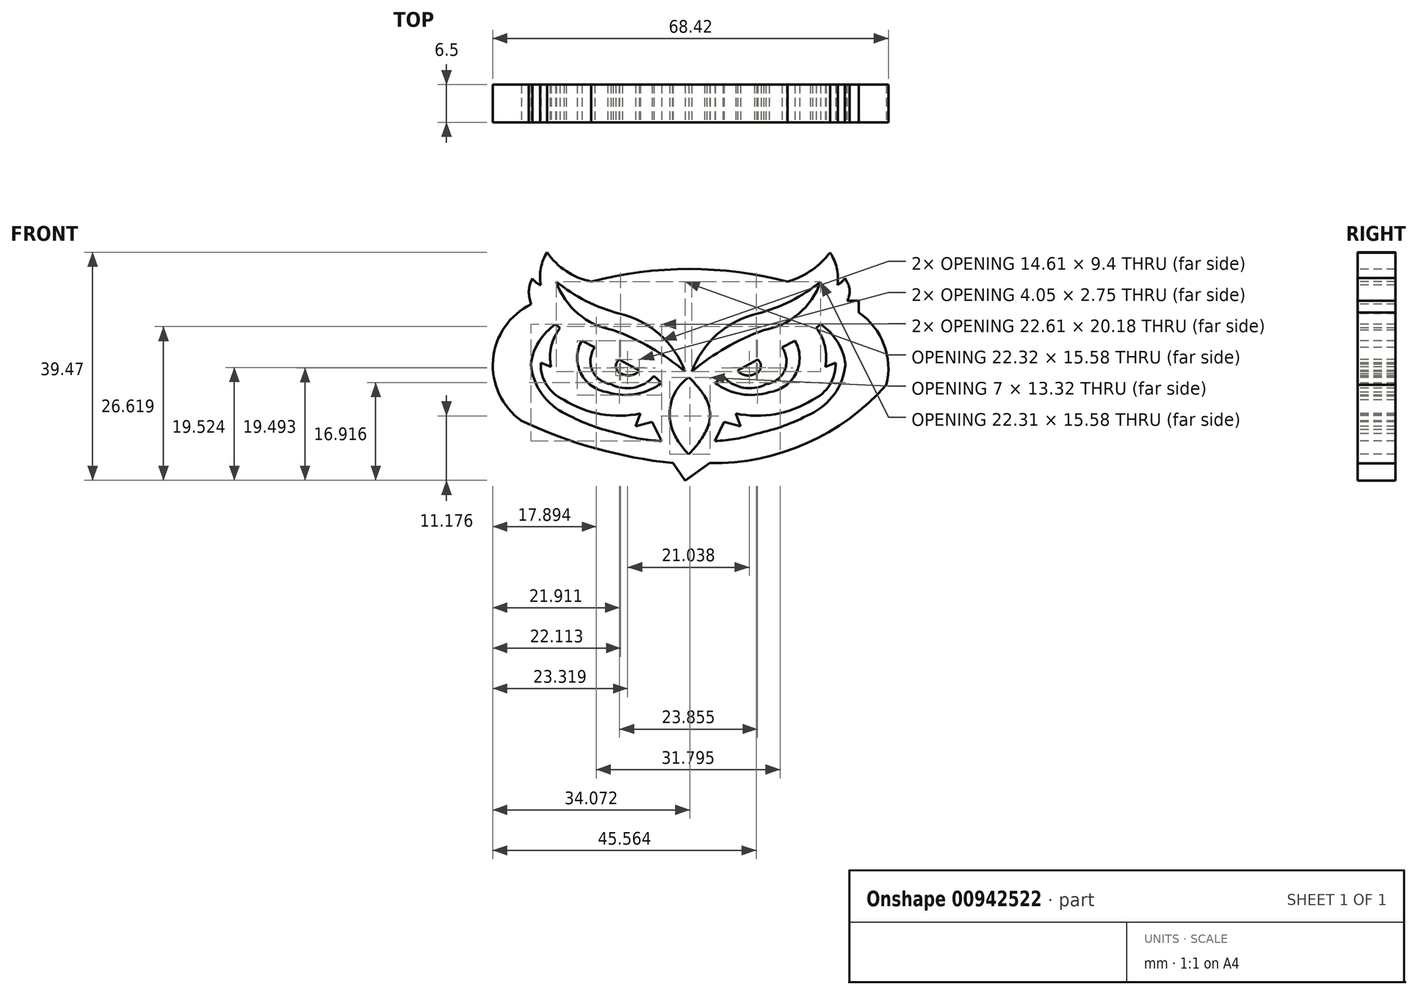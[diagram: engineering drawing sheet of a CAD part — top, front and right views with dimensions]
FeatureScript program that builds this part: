
annotation { "Feature Type Name" : "Feature", "Feature Type Description" : "" }
export const myFeature = defineFeature(function(context is Context, id is Id, definition is map)
    precondition{}
    {
        {
            var Q0;
            Q0=qCreatedBy(makeId("Front.planeOp"),FACE);
            var sketch = newSketch(context, id + "F0", { "sketchPlane" : qUnion([Q0])});
            skArc(sketch, "E0", {"start": v(-26.6, 12.43) * mm, "mid": v(-33.23, 2.83) * mm, "end": v(-28.3, -7.74) * mm});
            skArc(sketch, "E1", {"start": v(-28.3, -7.74) * mm, "mid": v(-15.5, -12.5) * mm, "end": v(-2.1, -15.07) * mm});
            skLineSegment(sketch, "E2", {"start": v(-2.1, -15.07) * mm, "end": v(0, -18.05) * mm});
            skLineSegment(sketch, "E3", {"start": v(0, -18.05) * mm, "end": v(4.24, -15.07) * mm});
            skArc(sketch, "E4", {"start": v(4.24, -15.07) * mm, "mid": v(21.01, -11.63) * mm, "end": v(34.81, -1.5) * mm});
            skArc(sketch, "E5", {"start": v(34.81, -1.5) * mm, "mid": v(34.38, 5.5) * mm, "end": v(30.06, 11) * mm});
            skLineSegment(sketch, "E6", {"start": v(30.06, 11) * mm, "end": v(30.06, 13.03) * mm});
            skLineSegment(sketch, "E7", {"start": v(30.06, 13.03) * mm, "end": v(28.03, 13.03) * mm});
            skArc(sketch, "E8", {"start": v(28.03, 13.03) * mm, "mid": v(28.46, 14.66) * mm, "end": v(28.03, 16.29) * mm});
            skLineSegment(sketch, "E9", {"start": v(28.03, 16.29) * mm, "end": v(27.65, 16.94) * mm});
            skArc(sketch, "E10", {"start": v(26.34, 15.79) * mm, "mid": v(27.07, 16.28) * mm, "end": v(27.65, 16.94) * mm});
            skArc(sketch, "E11", {"start": v(26.34, 15.79) * mm, "mid": v(26.23, 18.7) * mm, "end": v(25.06, 21.37) * mm});
            skArc(sketch, "E12", {"start": v(18.13, 16.5) * mm, "mid": v(21.98, 18.39) * mm, "end": v(25.06, 21.37) * mm});
            skLineSegment(sketch, "E13", {"start": v(18.13, 16.5) * mm, "end": v(17.7, 16.36) * mm});
            skArc(sketch, "E14", {"start": v(17.7, 16.36) * mm, "mid": v(0.72, 18.53) * mm, "end": v(-16.27, 16.36) * mm});
            skPoint(sketch, "E15", {"position": v(-26.6, 12.43) * mm});
            skArc(sketch, "E16", {"start": v(-26.44, 16.9) * mm, "mid": v(-27.02, 14.68) * mm, "end": v(-26.6, 12.43) * mm});
            skArc(sketch, "E17", {"start": v(-26.44, 16.9) * mm, "mid": v(-25.8, 16.21) * mm, "end": v(-24.98, 15.74) * mm});
            skArc(sketch, "E18", {"start": v(-23.87, 21.42) * mm, "mid": v(-24.96, 18.69) * mm, "end": v(-24.98, 15.74) * mm});
            skArc(sketch, "E19", {"start": v(-23.87, 21.42) * mm, "mid": v(-20.57, 18.14) * mm, "end": v(-16.27, 16.36) * mm});
            skArc(sketch, "E20", {"start": v(-22.31, 16.36) * mm, "mid": v(-17.14, 13) * mm, "end": v(-11.36, 10.82) * mm});
            skArc(sketch, "E21", {"start": v(0, 0.78) * mm, "mid": v(-4.42, 7.23) * mm, "end": v(-11.36, 10.82) * mm});
            skArc(sketch, "E22", {"start": v(0, 0.78) * mm, "mid": v(-5.9, 4.91) * mm, "end": v(-12.44, 7.97) * mm});
            skArc(sketch, "E23", {"start": v(-22.31, 16.36) * mm, "mid": v(-18.53, 10.81) * mm, "end": v(-12.44, 7.97) * mm});
            skArc(sketch, "E24.MirrorCS", {"start": v(1.14, 0.78) * mm, "mid": v(5.55, 7.23) * mm, "end": v(12.5, 10.82) * mm});
            skArc(sketch, "E25.MirrorCS", {"start": v(1.14, 0.78) * mm, "mid": v(7.04, 4.91) * mm, "end": v(13.58, 7.97) * mm});
            skArc(sketch, "E26.MirrorCS", {"start": v(23.45, 16.36) * mm, "mid": v(19.66, 10.81) * mm, "end": v(13.58, 7.97) * mm});
            skArc(sketch, "E27.MirrorCS", {"start": v(23.45, 16.36) * mm, "mid": v(18.27, 13) * mm, "end": v(12.5, 10.82) * mm});
            skArc(sketch, "E28", {"start": v(-17.86, 6.14) * mm, "mid": v(-18.04, 0.49) * mm, "end": v(-13.41, -2.76) * mm});
            skArc(sketch, "E29", {"start": v(-13.41, -2.76) * mm, "mid": v(-8.54, -3.12) * mm, "end": v(-4.05, -1.16) * mm});
            skLineSegment(sketch, "E30", {"start": v(-17.86, 6.14) * mm, "end": v(-15.64, 4.94) * mm});
            skLineSegment(sketch, "E31", {"start": v(-4.05, -1.16) * mm, "end": v(-5.42, 0) * mm});
            skArc(sketch, "E32", {"start": v(-15.64, 4.94) * mm, "mid": v(-16.05, 0.98) * mm, "end": v(-12.84, -1.4) * mm});
            skArc(sketch, "E33", {"start": v(-12.84, -1.4) * mm, "mid": v(-8.89, -2) * mm, "end": v(-5.42, 0) * mm});
            skArc(sketch, "E34.MirrorCS", {"start": v(13.98, -1.4) * mm, "mid": v(10.03, -2) * mm, "end": v(6.56, 0) * mm});
            skArc(sketch, "E35.MirrorCS", {"start": v(16.77, 4.94) * mm, "mid": v(17.19, 0.98) * mm, "end": v(13.98, -1.4) * mm});
            skLineSegment(sketch, "E36.MirrorCS", {"start": v(19, 6.14) * mm, "end": v(16.77, 4.94) * mm});
            skArc(sketch, "E37.MirrorCS", {"start": v(19, 6.14) * mm, "mid": v(19.17, 0.49) * mm, "end": v(14.55, -2.76) * mm});
            skArc(sketch, "E38.MirrorCS", {"start": v(14.55, -2.76) * mm, "mid": v(9.67, -3.12) * mm, "end": v(5.2, -1.16) * mm});
            skLineSegment(sketch, "E39.MirrorCS", {"start": v(5.2, -1.16) * mm, "end": v(6.56, 0) * mm});
            skArc(sketch, "E40", {"start": v(-11.43, 2.85) * mm, "mid": v(-11.94, 1.42) * mm, "end": v(-10.84, 0.37) * mm});
            skArc(sketch, "E41", {"start": v(-10.84, 0.37) * mm, "mid": v(-9.27, 0.15) * mm, "end": v(-7.93, 0.98) * mm});
            skLineSegment(sketch, "E42", {"start": v(-7.93, 0.98) * mm, "end": v(-11.43, 2.85) * mm});
            skLineSegment(sketch, "E43.MirrorCS", {"start": v(9.06, 0.98) * mm, "end": v(12.56, 2.85) * mm});
            skArc(sketch, "E44.MirrorCS", {"start": v(11.98, 0.37) * mm, "mid": v(10.4, 0.15) * mm, "end": v(9.06, 0.98) * mm});
            skArc(sketch, "E45.MirrorCS", {"start": v(12.56, 2.85) * mm, "mid": v(13.08, 1.42) * mm, "end": v(11.98, 0.37) * mm});
            skArc(sketch, "E46", {"start": v(24.24, 1.6) * mm, "mid": v(24.2, 5.13) * mm, "end": v(22.7, 8.34) * mm});
            skLineSegment(sketch, "E47", {"start": v(24.24, 1.6) * mm, "end": v(26.02, 2.32) * mm});
            skLineSegment(sketch, "E48", {"start": v(22.7, 8.34) * mm, "end": v(23.43, 8.95) * mm});
            skArc(sketch, "E49", {"start": v(27.72, 2.02) * mm, "mid": v(26.34, 5.96) * mm, "end": v(23.43, 8.95) * mm});
            skArc(sketch, "E50", {"start": v(21.63, -6.56) * mm, "mid": v(25.82, -3.08) * mm, "end": v(27.72, 2.02) * mm});
            skArc(sketch, "E51", {"start": v(12.41, -9.95) * mm, "mid": v(17.14, -8.58) * mm, "end": v(21.63, -6.56) * mm});
            skArc(sketch, "E52", {"start": v(5.12, -11.22) * mm, "mid": v(8.8, -10.84) * mm, "end": v(12.41, -9.95) * mm});
            skLineSegment(sketch, "E53", {"start": v(5.12, -11.22) * mm, "end": v(6.74, -7.9) * mm});
            skLineSegment(sketch, "E54", {"start": v(6.74, -7.9) * mm, "end": v(9.61, -8.71) * mm});
            skLineSegment(sketch, "E55", {"start": v(9.61, -8.71) * mm, "end": v(8.76, -6.47) * mm});
            skArc(sketch, "E56", {"start": v(8.76, -6.47) * mm, "mid": v(15.63, -6.58) * mm, "end": v(22.02, -4.1) * mm});
            skArc(sketch, "E57", {"start": v(22.02, -4.1) * mm, "mid": v(25.01, -1.5) * mm, "end": v(26.02, 2.32) * mm});
            skLineSegment(sketch, "E58.MirrorCS", {"start": v(-4.07, -11.22) * mm, "end": v(-5.7, -7.9) * mm});
            skArc(sketch, "E59.MirrorCS", {"start": v(-4.07, -11.22) * mm, "mid": v(-7.77, -10.84) * mm, "end": v(-11.37, -9.95) * mm});
            skArc(sketch, "E60.MirrorCS", {"start": v(-11.37, -9.95) * mm, "mid": v(-16.1, -8.58) * mm, "end": v(-20.59, -6.56) * mm});
            skArc(sketch, "E61.MirrorCS", {"start": v(-20.59, -6.56) * mm, "mid": v(-24.78, -3.08) * mm, "end": v(-26.68, 2.02) * mm});
            skArc(sketch, "E62.MirrorCS", {"start": v(-7.72, -6.47) * mm, "mid": v(-14.58, -6.58) * mm, "end": v(-20.98, -4.1) * mm});
            skLineSegment(sketch, "E63.MirrorCS", {"start": v(-5.7, -7.9) * mm, "end": v(-8.57, -8.71) * mm});
            skLineSegment(sketch, "E64.MirrorCS", {"start": v(-8.57, -8.71) * mm, "end": v(-7.72, -6.47) * mm});
            skArc(sketch, "E65.MirrorCS", {"start": v(-20.98, -4.1) * mm, "mid": v(-23.97, -1.5) * mm, "end": v(-24.98, 2.32) * mm});
            skLineSegment(sketch, "E66.MirrorCS", {"start": v(-23.2, 1.6) * mm, "end": v(-24.98, 2.32) * mm});
            skArc(sketch, "E67.MirrorCS", {"start": v(-23.2, 1.6) * mm, "mid": v(-23.15, 5.13) * mm, "end": v(-21.65, 8.34) * mm});
            skLineSegment(sketch, "E68.MirrorCS", {"start": v(-21.65, 8.34) * mm, "end": v(-22.4, 8.95) * mm});
            skArc(sketch, "E69.MirrorCS", {"start": v(-26.68, 2.02) * mm, "mid": v(-25.3, 5.96) * mm, "end": v(-22.4, 8.95) * mm});
            skArc(sketch, "E70", {"start": v(-2.23, -9.26) * mm, "mid": v(-1.03, -11.54) * mm, "end": v(0.62, -13.53) * mm});
            skArc(sketch, "E71", {"start": v(0.62, -13.53) * mm, "mid": v(2.35, -11.51) * mm, "end": v(3.74, -9.26) * mm});
            skArc(sketch, "E72", {"start": v(3.74, -9.26) * mm, "mid": v(4.3, -6.31) * mm, "end": v(3.38, -3.46) * mm});
            skArc(sketch, "E73", {"start": v(3.38, -3.46) * mm, "mid": v(2.1, -1.75) * mm, "end": v(0.62, -0.22) * mm});
            skArc(sketch, "E74", {"start": v(0.62, -0.22) * mm, "mid": v(-2.34, -4.25) * mm, "end": v(-2.23, -9.26) * mm});
            skSolve(sketch);
        }
        {
            var Q0;
            Q0 = qSketchRegion(id + "F0", true);
            extrude(context, id + "F1", {"entities" : qUnion([Q0]), "oppositeDirection" : true, "depth" : 6.5 * mm, "offsetDistance" : 25.4 * mm});
        }
    });
